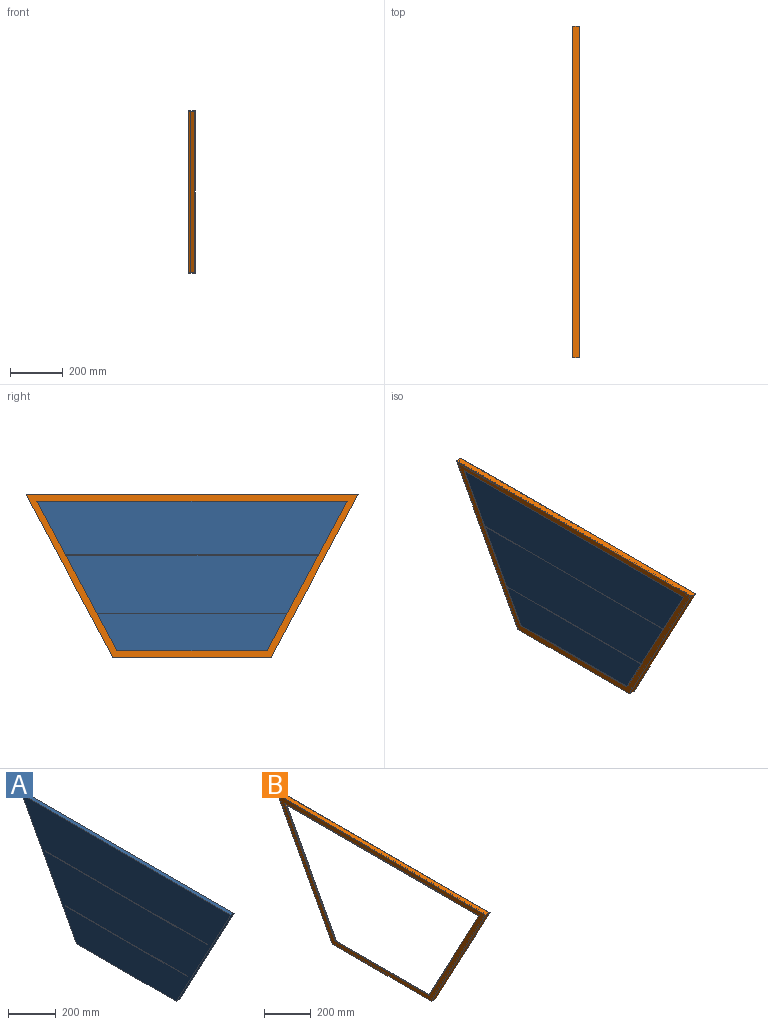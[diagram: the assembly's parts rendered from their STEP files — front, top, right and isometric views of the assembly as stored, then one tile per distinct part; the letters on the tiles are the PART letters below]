
ASSEMBLY  parts=2 mates=1
PART A: 14 faces, bbox 20x1238.3x604.3 mm
  f0: plane 1238.31x604.32mm, normal (1,0,0), area 549728.2mm2, adj f2,f3,f4,f5,f6,f7,f8,f9
  f1: plane 1238.31x604.32mm, normal (-1,0,0), area 549728.2mm2, adj f2,f3,f4,f5,f6,f7,f8,f9
  f2: plane 1238.31x20mm, normal (0,0,1), area 24766.2mm2, adj f0,f1,f3,f5
  f3: plane 604.32x322.94mm, normal (0,-0.88,-0.47), area 13703.8mm2, adj f0,f1,f2,f4
  f4: plane 592.17x20mm, normal (0,0,-1), area 11843.4mm2, adj f0,f1,f3,f5
  f5: plane 604.32x323.2mm, normal (0,0.88,-0.47), area 13706.3mm2, adj f0,f1,f2,f4
  f6: plane 723.81x20mm, normal (0,0,-1), area 14476.1mm2, adj f0,f1,f7,f9
  f7: plane 20x2mm, normal (0,0.88,0.47), area 45.4mm2, adj f0,f1,f6,f8
  f8: plane 721.67x20mm, normal (0,0,1), area 14433.4mm2, adj f0,f1,f7,f9
  f9: plane 20x2mm, normal (0,-0.88,0.47), area 45.4mm2, adj f0,f1,f6,f8
  f10: plane 961.15x20mm, normal (0,0,-1), area 19223mm2, adj f0,f1,f11,f13
  f11: plane 20x2mm, normal (0,0.88,0.47), area 45.4mm2, adj f0,f1,f10,f12
  f12: plane 959.01x20mm, normal (0,0,1), area 19180.2mm2, adj f0,f1,f11,f13
  f13: plane 20x2mm, normal (0,-0.88,0.47), area 45.4mm2, adj f0,f1,f10,f12
PART B: 27 faces, bbox 25x1260x617.3 mm
  f0: cylinder r=2.02mm len=616.28mm, axis (0,-0.47,0.88), area 2177.2mm2, adj f1,f6,f18,f19
  f1: plane 611.33x326.79mm, normal (0,0.88,0.47), area 11437.7mm2, adj f0,f2,f7,f20
  f2: cylinder r=3.5mm len=612.98mm, axis (0,-0.47,0.88), area 3795.2mm2, adj f1,f8,f21,f22
  f3: cylinder r=2.02mm len=572.28mm, axis (0,-0.47,0.88), area 2020.8mm2, adj f4,f9,f22,f23
  f4: plane 567.33x303.27mm, normal (0,0.88,0.47), area 643.3mm2, adj f3,f10,f24,f25
  f5: plane 617.33x330mm, normal (0,-0.88,-0.47), area 17500mm2, adj f11,f18,f25,f26
  f6: cylinder r=2.02mm len=598.8mm, axis (0,-1,0), area 1871.4mm2, adj f0,f7,f12,f18
  f7: plane 596.4x16.5mm, normal (0,0,1), area 9840.7mm2, adj f1,f6,f8,f13
  f8: cylinder r=3.5mm len=596.4mm, axis (0,-1,0), area 3270.5mm2, adj f2,f7,f14,f22
  f9: cylinder r=2.02mm len=572.43mm, axis (0,-1,0), area 1788.8mm2, adj f3,f10,f15,f22
  f10: plane 570.03x1mm, normal (0,0,1), area 570mm2, adj f4,f9,f16,f25
  f11: plane 600x25mm, normal (0,0,-1), area 15000mm2, adj f5,f17,f18,f25
  f12: cylinder r=2.02mm len=616.28mm, axis (0,-0.47,-0.88), area 2177.2mm2, adj f6,f13,f18,f19
  f13: plane 611.33x326.79mm, normal (0,-0.88,0.47), area 11437.7mm2, adj f7,f12,f14,f20
  f14: cylinder r=3.5mm len=612.98mm, axis (0,-0.47,-0.88), area 3795.2mm2, adj f8,f13,f21,f22
  f15: cylinder r=2.02mm len=572.28mm, axis (0,-0.47,-0.88), area 2020.8mm2, adj f9,f16,f22,f23
  f16: plane 567.33x303.27mm, normal (0,-0.88,0.47), area 643.3mm2, adj f10,f15,f24,f25
  f17: plane 617.33x330mm, normal (0,0.88,-0.47), area 17500mm2, adj f11,f18,f25,f26
  f18: plane 1260x617.33mm, normal (1,0,0), area 3255.5mm2, adj f0,f5,f6,f11,f12,f17,f19,f26
  f19: cylinder r=2.02mm len=1256.66mm, axis (0,1,0), area 3924.2mm2, adj f0,f12,f18,f20
  f20: plane 1249.99x16.5mm, normal (0,0,-1), area 20624.8mm2, adj f1,f13,f19,f21
  f21: cylinder r=3.5mm len=1249.99mm, axis (0,1,0), area 6848.9mm2, adj f2,f14,f20,f22
  f22: plane 1238.31x604.33mm, normal (1,0,0), area 51582.3mm2, adj f2,f3,f8,f9,f14,f15,f21,f23
  f23: cylinder r=2.02mm len=1183.25mm, axis (0,1,0), area 3694.2mm2, adj f3,f15,f22,f24
  f24: plane 1176.58x1mm, normal (0,0,-1), area 1176.6mm2, adj f4,f16,f23,f25
  f25: plane 1260x617.33mm, normal (-1,0,0), area 78665.2mm2, adj f4,f5,f10,f11,f16,f17,f24,f26
  f26: plane 1260x25mm, normal (0,0,1), area 31500mm2, adj f5,f17,f18,f25
PLACE A t=(177.46,-249.06,-142.55)mm
PLACE B t=(177.46,-249.11,-140.79)mm
MATE fastened B.f22 <-> A.f1  axis (1,0,0) through (180.46,-249.11,-415.35)mm
